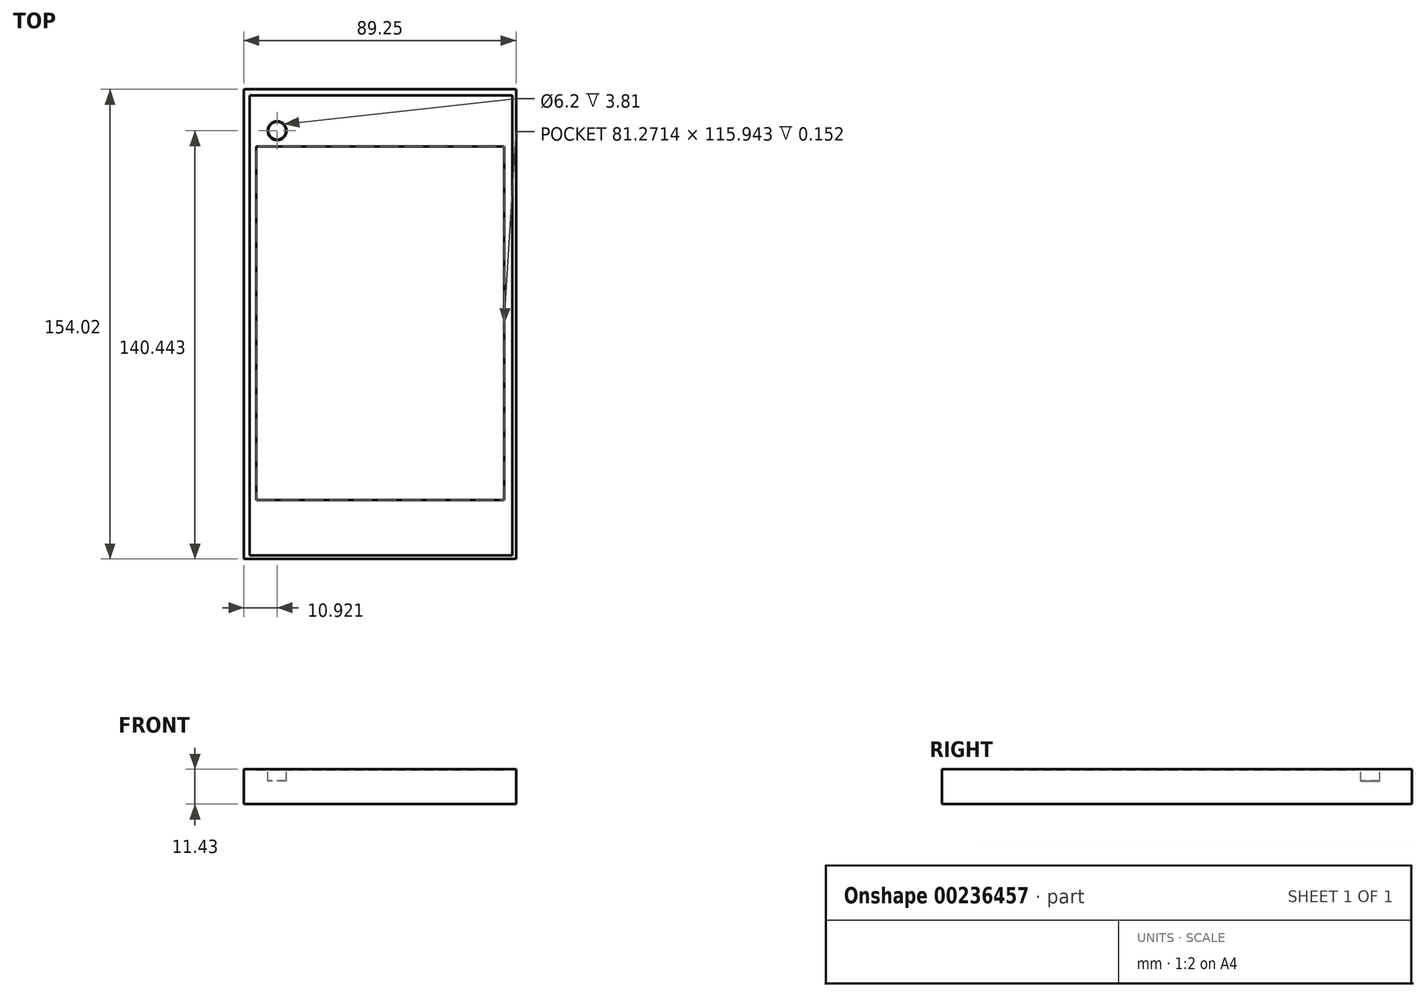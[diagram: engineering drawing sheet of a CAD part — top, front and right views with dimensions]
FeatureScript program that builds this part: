
annotation { "Feature Type Name" : "Feature", "Feature Type Description" : "" }
export const myFeature = defineFeature(function(context is Context, id is Id, definition is map)
    precondition{}
    {
        {
            var Q0;
            Q0=qCreatedBy(makeId("Top.planeOp"),FACE);
            var sketch = newSketch(context, id + "F0", { "sketchPlane" : qUnion([Q0])});
            skLineSegment(sketch, "E0.top", {"start": v(0, 76.43) * mm, "end": v(-41.66, 76.43) * mm});
            skLineSegment(sketch, "E0.right", {"start": v(-41.66, 0) * mm, "end": v(-41.66, 76.43) * mm});
            skLineSegment(sketch, "E1.top", {"start": v(-41.66, -76.72) * mm, "end": v(0, -76.72) * mm});
            skLineSegment(sketch, "E1.left", {"start": v(-41.66, 0) * mm, "end": v(-41.66, -76.72) * mm});
            skLineSegment(sketch, "E2.bottom", {"start": v(0, 76.43) * mm, "end": v(47.6, 76.43) * mm});
            skLineSegment(sketch, "E2.top", {"start": v(0, -77.6) * mm, "end": v(47.6, -77.6) * mm});
            skLineSegment(sketch, "E2.right", {"start": v(47.6, 76.43) * mm, "end": v(47.6, -77.6) * mm});
            skLineSegment(sketch, "E3.bottom", {"start": v(-41.66, 76.43) * mm, "end": v(47.6, 76.43) * mm});
            skLineSegment(sketch, "E3.top", {"start": v(-41.66, -77.6) * mm, "end": v(47.6, -77.6) * mm});
            skLineSegment(sketch, "E3.left", {"start": v(-41.66, 76.43) * mm, "end": v(-41.66, -77.6) * mm});
            skSolve(sketch);
        }
        {
            var Q0;
            Q0 = qSketchRegion(id + "F0", true);
            extrude(context, id + "F1", {"entities" : qUnion([Q0]), "depth" : 11.43 * mm});
        }
        {
            var Q0;
            Q0=makeQuery(id+"F1.opExtrude","CAP_FACE",FACE,{"disambiguationData":[OSD([sQuery(id+"F0.wireOp",EDGE,"E3.bottom"),sQuery(id+"F0.wireOp",EDGE,"E3.top"),sQuery(id+"F0.wireOp",EDGE,"E3.left"),sQuery(id+"F0.wireOp",EDGE,"E2.right")])],"isStart":false});
            var sketch = newSketch(context, id + "F2", { "sketchPlane" : qUnion([Q0])});
            skLineSegment(sketch, "E4.bottom", {"start": v(-37.62, -58.32) * mm, "end": v(43.65, -58.32) * mm});
            skLineSegment(sketch, "E4.top", {"start": v(-37.62, 57.62) * mm, "end": v(43.65, 57.62) * mm});
            skLineSegment(sketch, "E4.left", {"start": v(-37.62, -58.32) * mm, "end": v(-37.62, 57.62) * mm});
            skLineSegment(sketch, "E4.right", {"start": v(43.65, -58.32) * mm, "end": v(43.65, 57.62) * mm});
            skSolve(sketch);
        }
        {
            var Q0;
            Q0 = qSketchRegion(id + "F2", true);
            extrude(context, id + "F3", {"entities" : qUnion([Q0]), "operationType" : NewBodyOperationType.REMOVE, "oppositeDirection" : true, "depth" : 0.18 * mm});
        }
        {
            var Q0;
            Q0=makeQuery(id+"F1.opExtrude","CAP_FACE",FACE,{"disambiguationData":[OSD([sQuery(id+"F0.wireOp",EDGE,"E3.bottom"),sQuery(id+"F0.wireOp",EDGE,"E3.top"),sQuery(id+"F0.wireOp",EDGE,"E3.left"),sQuery(id+"F0.wireOp",EDGE,"E2.right")])],"isStart":false});
            var sketch = newSketch(context, id + "F4", { "sketchPlane" : qUnion([Q0])});
            skLineSegment(sketch, "E5.bottom", {"start": v(-39.8, 74.44) * mm, "end": v(46.4, 74.44) * mm});
            skLineSegment(sketch, "E5.top", {"start": v(-39.8, -76.44) * mm, "end": v(46.4, -76.44) * mm});
            skLineSegment(sketch, "E5.left", {"start": v(-39.8, 74.44) * mm, "end": v(-39.8, -76.44) * mm});
            skLineSegment(sketch, "E5.right", {"start": v(46.4, 74.44) * mm, "end": v(46.4, -76.44) * mm});
            skSolve(sketch);
        }
        {
            var Q0;
            Q0 = qSketchRegion(id + "F4", true);
            extrude(context, id + "F5", {"entities" : qUnion([Q0]), "operationType" : NewBodyOperationType.REMOVE, "oppositeDirection" : true, "depth" : 0.03 * mm});
        }
        {
            var Q0;
            Q0=makeQuery(id+"F5.boolean.opBoolean","COPY",FACE,{"derivedFrom":makeQuery(id+"F5.opExtrude","CAP_FACE",FACE,{"disambiguationData":[OSD([sQuery(id+"F4.wireOp",EDGE,"E5.bottom"),sQuery(id+"F4.wireOp",EDGE,"E5.top"),sQuery(id+"F4.wireOp",EDGE,"E5.left"),sQuery(id+"F4.wireOp",EDGE,"E5.right")])],"isStart":false})});
            var sketch = newSketch(context, id + "F6", { "sketchPlane" : qUnion([Q0])});
            skCircle(sketch, "E6", {"center": v(-30.74, 62.85) * mm, "radius": 3.1 * mm});
            skSolve(sketch);
        }
        {
            var Q0;
            Q0 = qSketchRegion(id + "F6", true);
            extrude(context, id + "F7", {"entities" : qUnion([Q0]), "operationType" : NewBodyOperationType.REMOVE, "oppositeDirection" : true, "depth" : 3.8 * mm});
        }
        {
            var Q0;
            Q0=makeQuery(id+"F7.boolean.opBoolean","COPY",FACE,{"derivedFrom":makeQuery(id+"F7.opExtrude","CAP_FACE",FACE,{"disambiguationData":[OSD([sQuery(id+"F6.wireOp",EDGE,"E6")])],"isStart":false})});
            var sketch = newSketch(context, id + "F8", { "sketchPlane" : qUnion([Q0])});
            skCircle(sketch, "E7", {"center": v(-30.74, 62.85) * mm, "radius": 2.93 * mm});
            skSolve(sketch);
        }
        {
            var Q0;
            Q0 = qSketchRegion(id + "F8", true);
            extrude(context, id + "F9", {"entities" : qUnion([Q0]), "operationType" : NewBodyOperationType.ADD, "depth" : 0.03 * mm});
        }
    });
